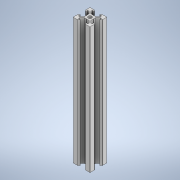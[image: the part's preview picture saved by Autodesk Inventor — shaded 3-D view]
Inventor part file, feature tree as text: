
AUTODESK INVENTOR PART (.ipt)
format: ipt  version: 2021 (Build 250183000, 183)  size: 233,984 bytes
history: native  units: mm
features: sketch x3, extrude x2, fillet x2, other x1, pattern_circular x1, hole x1, projected_geometry x1
ambient origin geometry x8: Origin, YZ Plane, XZ Plane, XY Plane, X Axis, Y Axis, Z Axis, Center Point
bodies: Body1 (feature_tree)
feature tree (11):
  other  "實體1"
  extrude  "擠出1"  Depth=20.0mm
  extrude  "擠出2"  Depth=20.0mm
  fillet  "圓角1"  Radius=150.0mm
  pattern_circular  "環形陣列1"  [2 undecoded]
  hole  "孔1"  [1 undecoded]
  fillet  "圓角2"  Radius=6.2mm
  sketch  "草圖1"
  sketch  "草圖2"
  projected_geometry  "投影迴路1"
  sketch  "草圖3"
note: 3 required parameter values undecoded (feature->parameter linkage not recoverable at this tier; creation-order binding heuristic only, values carry confidence <= 0.55)
